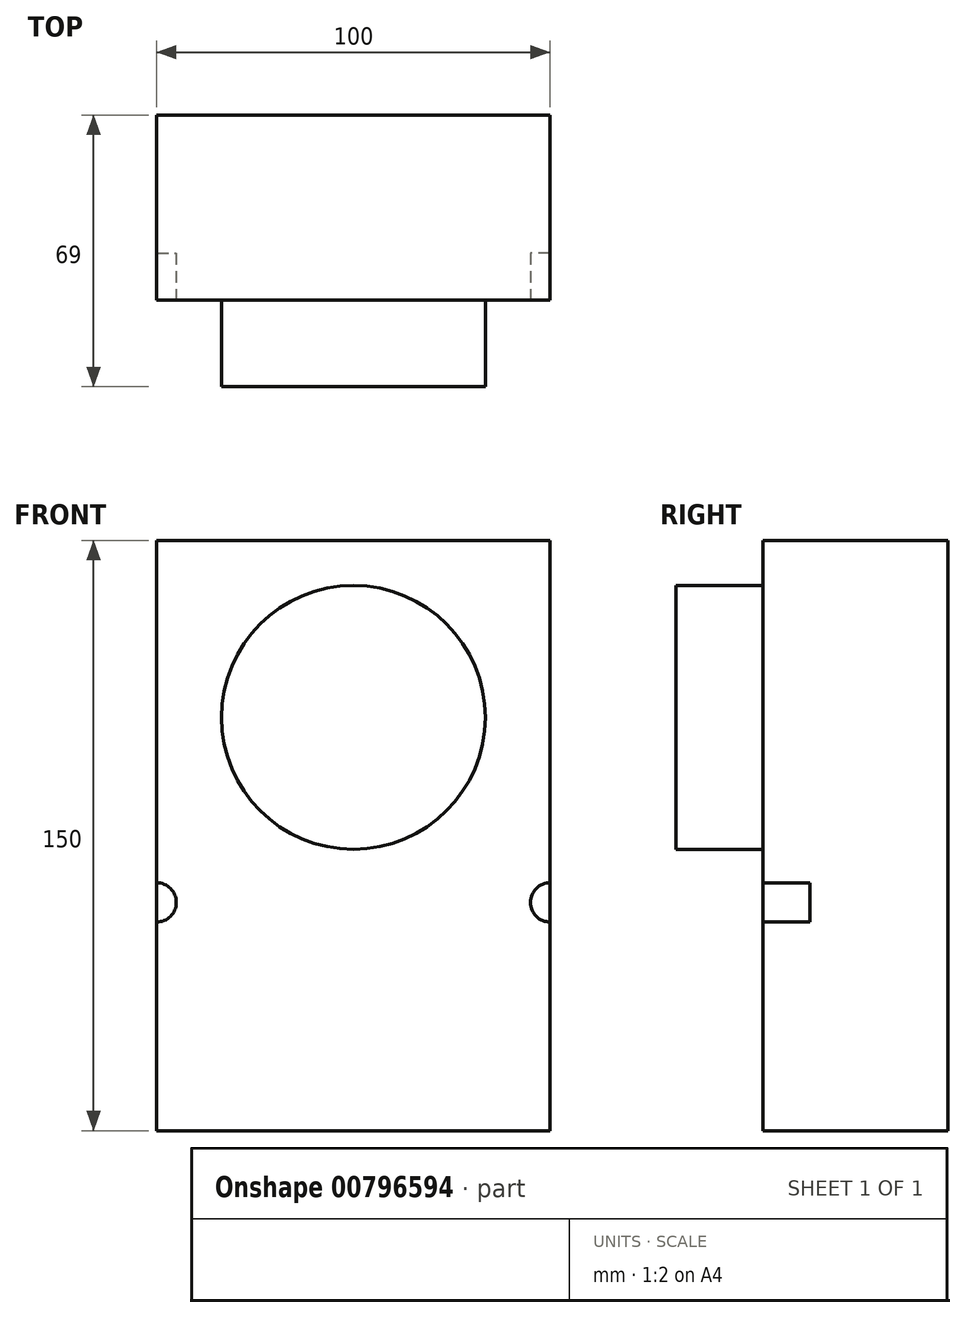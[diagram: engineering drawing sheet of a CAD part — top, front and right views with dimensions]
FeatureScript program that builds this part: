
annotation { "Feature Type Name" : "Feature", "Feature Type Description" : "" }
export const myFeature = defineFeature(function(context is Context, id is Id, definition is map)
    precondition{}
    {
        {
            var Q0;
            Q0=qCreatedBy(makeId("Front.planeOp"),FACE);
            var sketch = newSketch(context, id + "F0", { "sketchPlane" : qUnion([Q0])});
            skLineSegment(sketch, "E0.bottom", {"start": v(-50, 75) * mm, "end": v(50, 75) * mm});
            skLineSegment(sketch, "E0.top", {"start": v(-50, -75) * mm, "end": v(50, -75) * mm});
            skLineSegment(sketch, "E0.left", {"start": v(-50, 75) * mm, "end": v(-50, -75) * mm});
            skLineSegment(sketch, "E0.right", {"start": v(50, 75) * mm, "end": v(50, -75) * mm});
            skSolve(sketch);
        }
        {
            var Q0;
            Q0 = qSketchRegion(id + "F0", true);
            extrude(context, id + "F1", {"entities" : qUnion([Q0]), "depth" : 47 * mm, "offsetDistance" : 25 * mm});
        }
        {
            var Q0;
            Q0=makeQuery(id+"F1.opExtrude","CAP_FACE",FACE,{"disambiguationData":[OSD([sQuery(id+"F0.wireOp",EDGE,"E0.bottom"),sQuery(id+"F0.wireOp",EDGE,"E0.top"),sQuery(id+"F0.wireOp",EDGE,"E0.left"),sQuery(id+"F0.wireOp",EDGE,"E0.right")])],"isStart":false});
            var sketch = newSketch(context, id + "F2", { "sketchPlane" : qUnion([Q0])});
            skCircle(sketch, "E1", {"center": v(0, 30) * mm, "radius": 33.5 * mm});
            skSolve(sketch);
        }
        {
            var Q0;
            Q0 = qSketchRegion(id + "F2", true);
            extrude(context, id + "F3", {"entities" : qUnion([Q0]), "operationType" : NewBodyOperationType.ADD, "depth" : 22 * mm, "offsetDistance" : 25 * mm});
        }
        {
            var Q0;
            Q0=makeQuery(id+"F1.opExtrude","CAP_FACE",FACE,{"disambiguationData":[OSD([sQuery(id+"F0.wireOp",EDGE,"E0.bottom"),sQuery(id+"F0.wireOp",EDGE,"E0.top"),sQuery(id+"F0.wireOp",EDGE,"E0.left"),sQuery(id+"F0.wireOp",EDGE,"E0.right")])],"isStart":false});
            var sketch = newSketch(context, id + "F4", { "sketchPlane" : qUnion([Q0])});
            skCircle(sketch, "E2", {"center": v(50, -17) * mm, "radius": 5 * mm});
            skCircle(sketch, "E3", {"center": v(-50, -17) * mm, "radius": 5 * mm});
            skSolve(sketch);
        }
        {
            var Q0;
            Q0 = qSketchRegion(id + "F4", true);
            extrude(context, id + "F5", {"entities" : qUnion([Q0]), "operationType" : NewBodyOperationType.REMOVE, "oppositeDirection" : true, "depth" : 12 * mm, "offsetDistance" : 25 * mm});
        }
    });
